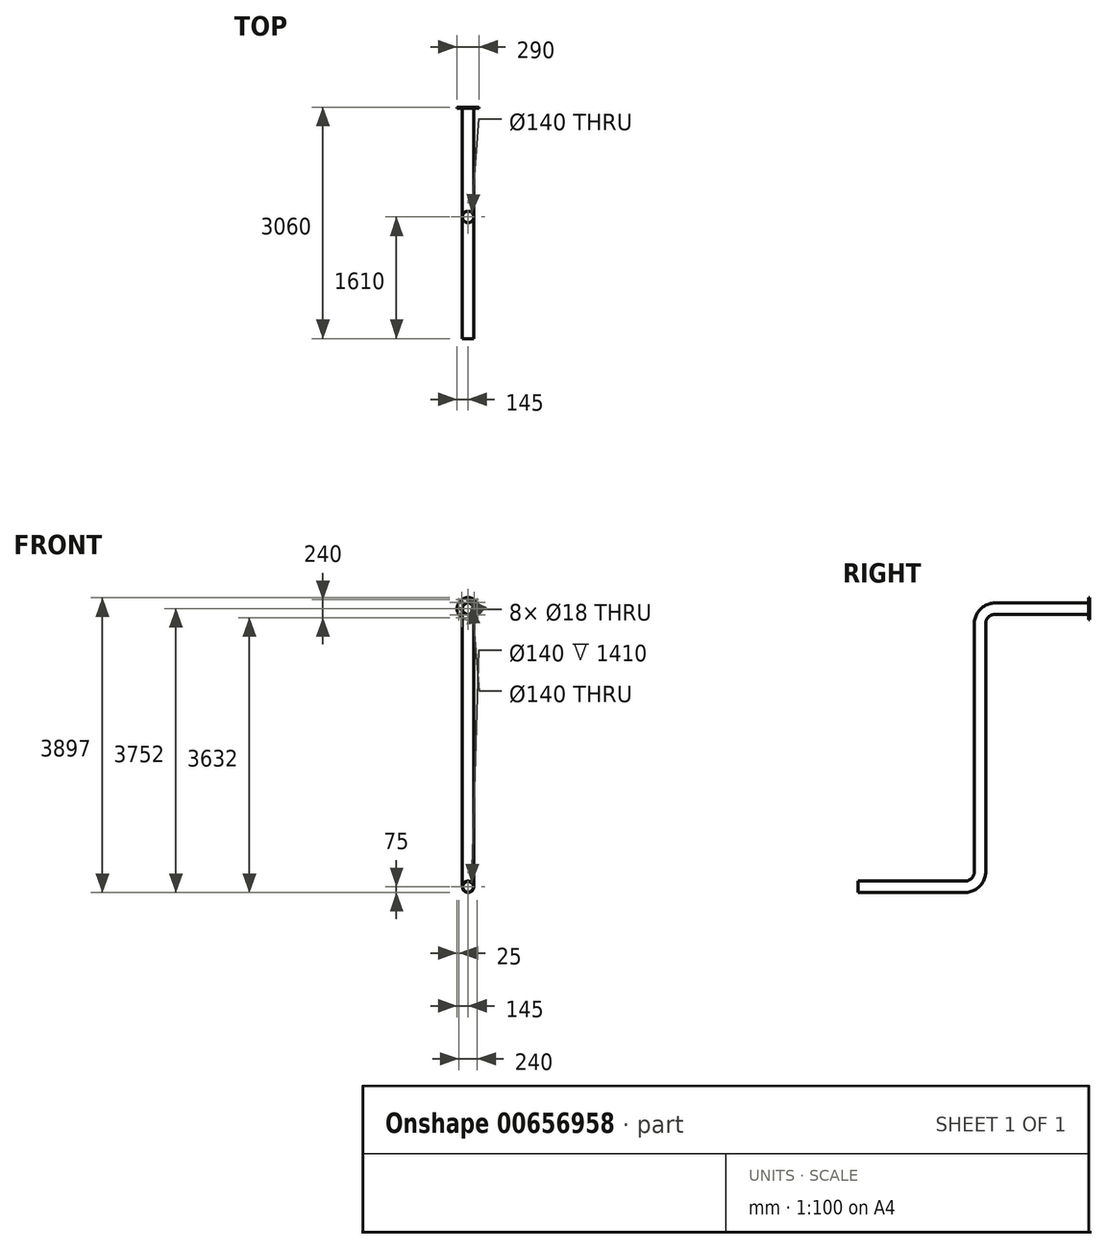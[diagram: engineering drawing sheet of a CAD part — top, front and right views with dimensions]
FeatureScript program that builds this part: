
annotation { "Feature Type Name" : "Feature", "Feature Type Description" : "" }
export const myFeature = defineFeature(function(context is Context, id is Id, definition is map)
    precondition{}
    {
        {
            var Q0;
            Q0=qCreatedBy(makeId("Front.planeOp"),FACE);
            var sketch = newSketch(context, id + "F0", { "sketchPlane" : qUnion([Q0])});
            skCircle(sketch, "E0", {"center": v(0, 0) * mm, "radius": 70 * mm});
            skCircle(sketch, "E1", {"center": v(0, 0) * mm, "radius": 75 * mm});
            skSolve(sketch);
        }
        {
            var Q0;
            Q0=qCreatedBy(makeId("Right.planeOp"),FACE);
            var sketch = newSketch(context, id + "F1", { "sketchPlane" : qUnion([Q0])});
            skLineSegment(sketch, "E2", {"start": v(0, 0) * mm, "end": v(-1250, 0) * mm});
            skLineSegment(sketch, "E3", {"start": v(-1450, -200) * mm, "end": v(-1450, -3477) * mm});
            skLineSegment(sketch, "E4", {"start": v(-1650, -3677) * mm, "end": v(-3060, -3677) * mm});
            skPoint(sketch, "E5.visualSharp", {"position": v(-1450, 0) * mm});
            skArc(sketch, "E5.filletArc", {"start": v(-1250, 0) * mm, "mid": v(-1391.42, -58.58) * mm, "end": v(-1450, -200) * mm});
            skPoint(sketch, "E6.visualSharp", {"position": v(-1450, -3677) * mm});
            skArc(sketch, "E6.filletArc", {"start": v(-1650, -3677) * mm, "mid": v(-1508.58, -3618.42) * mm, "end": v(-1450, -3477) * mm});
            skSolve(sketch);
        }
        {
            var Q0;
            Q0=makeQuery(id+"F0.imprint","IMPRINT",FACE,{"disambiguationData":[TD([[makeQuery(id+"F0.imprint","IMPRINT",EDGE,{"derivedFrom":sQuery(id+"F0.wireOp",EDGE,"E0")}),-1.0]])]});
            var Q1;
            Q1=sQuery(id+"F1.wireOp",EDGE,"E2");
            var Q2;
            Q2=sQuery(id+"F1.wireOp",EDGE,"E5.filletArc");
            var Q3;
            Q3=sQuery(id+"F1.wireOp",EDGE,"E3");
            var Q4;
            Q4=sQuery(id+"F1.wireOp",EDGE,"E6.filletArc");
            var Q5;
            Q5=sQuery(id+"F1.wireOp",EDGE,"E4");
            sweep(context, id + "F2", {"profiles" : qUnion([Q0]), "path" : qUnion([Q1, Q2, Q3, Q4, Q5])});
        }
        {
            var Q0;
            Q0=qCreatedBy(makeId("Front.planeOp"),FACE);
            var sketch = newSketch(context, id + "F3", { "sketchPlane" : qUnion([Q0])});
            skCircle(sketch, "E7", {"center": v(0, 0) * mm, "radius": 145 * mm});
            skCircle(sketch, "E8", {"center": v(0, 120) * mm, "radius": 9 * mm});
            skCircle(sketch, "E9.1.0", {"center": v(-84.85, 84.85) * mm, "radius": 9 * mm});
            skCircle(sketch, "E9.2.0", {"center": v(-120, 0) * mm, "radius": 9 * mm});
            skCircle(sketch, "E9.3.0", {"center": v(-84.85, -84.85) * mm, "radius": 9 * mm});
            skCircle(sketch, "E9.4.0", {"center": v(0, -120) * mm, "radius": 9 * mm});
            skCircle(sketch, "E9.5.0", {"center": v(84.85, -84.85) * mm, "radius": 9 * mm});
            skCircle(sketch, "E9.6.0", {"center": v(120, 0) * mm, "radius": 9 * mm});
            skCircle(sketch, "E9.7.0", {"center": v(84.85, 84.85) * mm, "radius": 9 * mm});
            skSolve(sketch);
        }
        {
            var Q0;
            Q0=makeQuery(id+"F3.imprint","IMPRINT",FACE,{"disambiguationData":[TD([[makeQuery(id+"F3.imprint","IMPRINT",EDGE,{"derivedFrom":sQuery(id+"F3.wireOp",EDGE,"E7")}),1.0]])]});
            extrude(context, id + "F4", {"entities" : qUnion([Q0]), "operationType" : NewBodyOperationType.ADD, "depth" : 15 * mm, "offsetDistance" : 25 * mm});
        }
        {
            var Q0;
            Q0=makeQuery(id+"F0.imprint","IMPRINT",FACE,{"disambiguationData":[TD([[makeQuery(id+"F0.imprint","IMPRINT",EDGE,{"derivedFrom":sQuery(id+"F0.wireOp",EDGE,"E0")}),1.0]])]});
            extrude(context, id + "F5", {"entities" : qUnion([Q0]), "operationType" : NewBodyOperationType.REMOVE, "depth" : 25 * mm, "offsetDistance" : 25 * mm});
        }
    });
